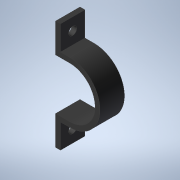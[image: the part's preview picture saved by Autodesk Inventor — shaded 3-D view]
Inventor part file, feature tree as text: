
AUTODESK INVENTOR PART (.ipt)
format: ipt  version: 2021 (Build 250183000, 183)  size: 285,696 bytes
history: native  units: mm
features: other x4, reference x3, extrude x2, sketch x2
ambient origin geometry x8: Origin, YZ Plane, XZ Plane, XY Plane, X Axis, Y Axis, Z Axis, Center Point
bodies: Volumenkörper1 (feature_tree)
feature tree (11):
  extrude  "Extrusion1"  Depth=2.4mm
  extrude  "Extrusion2"  Depth=12.5mm
  sketch  "Skizze1"  dims[d0=2.4mm d1=2.4mm]
  reference  "Referenz1"
  reference  "Referenz2"
  reference  "Referenz3"
  sketch  "Skizze2"  dims[d2=2.4mm d4=12.5mm d5=7.4mm d7=12.5mm d8=12.0mm d9=12.0mm d10=0.0mm d11=4.0mm d12=0.0mm d13=0.0mm]
  other  "<userpath>\Desktop\Bachelorarbeit\CAD\00_RobotAssembly.iam"
  other  "00_RobotAssembly.iam"
  other  "02_Motor:2"
  other  "01_CaseBottom:1"
